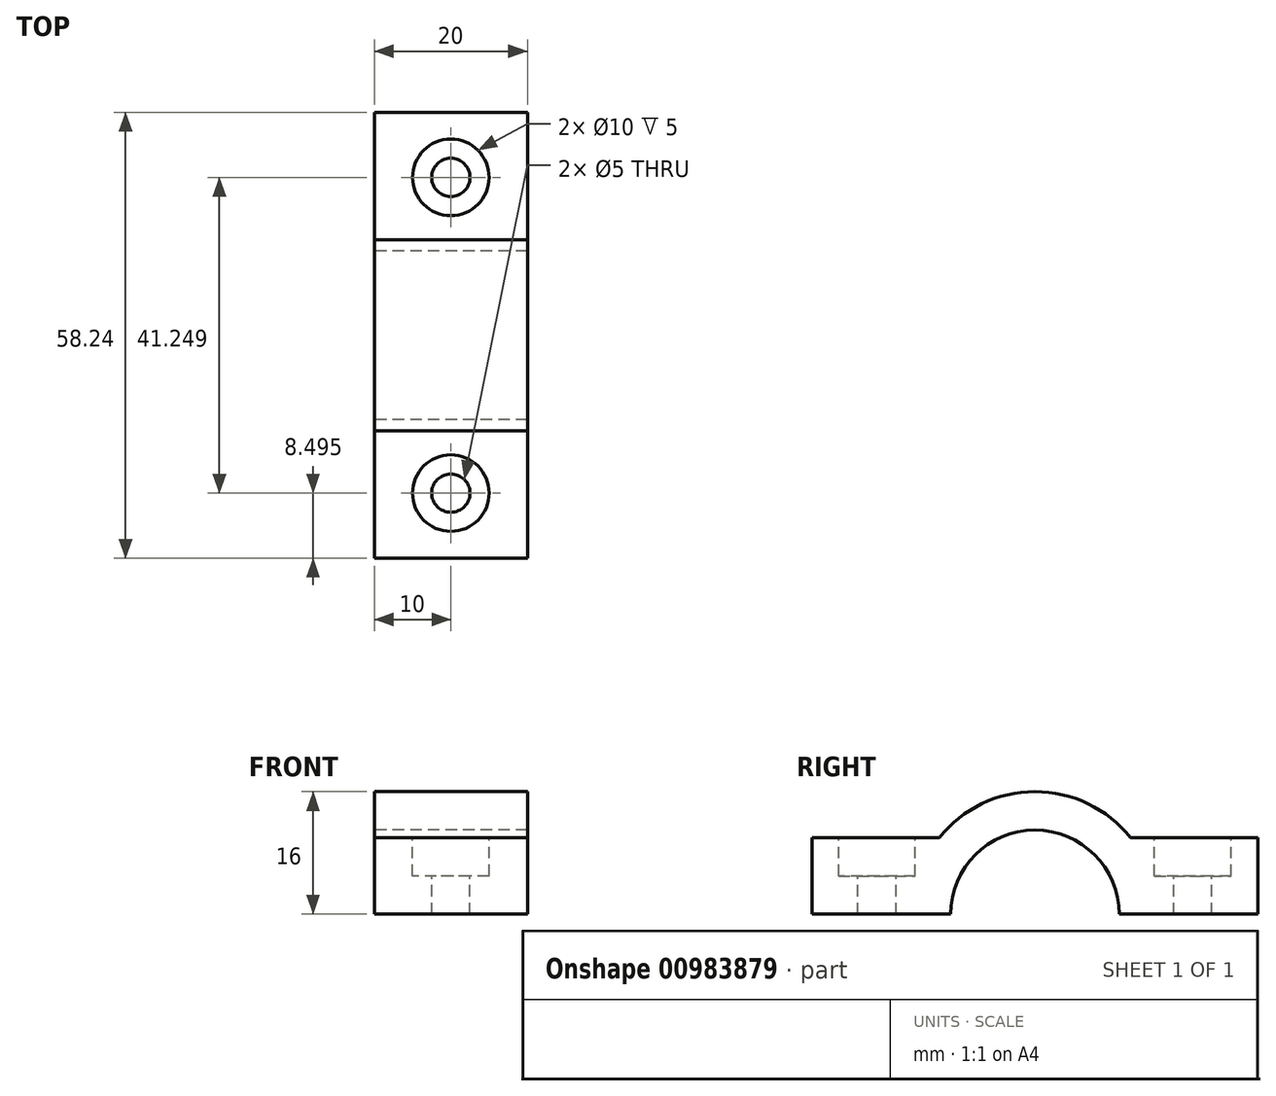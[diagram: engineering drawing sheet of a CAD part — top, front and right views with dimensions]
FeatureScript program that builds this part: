
annotation { "Feature Type Name" : "Feature", "Feature Type Description" : "" }
export const myFeature = defineFeature(function(context is Context, id is Id, definition is map)
    precondition{}
    {
        {
            var Q0;
            Q0=qCreatedBy(makeId("Right.planeOp"),FACE);
            var sketch = newSketch(context, id + "F0", { "sketchPlane" : qUnion([Q0])});
            skArc(sketch, "E0", {"start": v(11, 0) * mm, "mid": v(0, 11) * mm, "end": v(-11, 0) * mm});
            skLineSegment(sketch, "E1", {"start": v(11, 0) * mm, "end": v(29.12, 0) * mm});
            skLineSegment(sketch, "E2", {"start": v(-11, 0) * mm, "end": v(-29.12, 0) * mm});
            skLineSegment(sketch, "E3", {"start": v(29.12, 0) * mm, "end": v(29.12, 10) * mm});
            skLineSegment(sketch, "E4", {"start": v(-29.12, 0) * mm, "end": v(-29.12, 10) * mm});
            skLineSegment(sketch, "E5", {"start": v(-29.12, 10) * mm, "end": v(-12.49, 10) * mm});
            skLineSegment(sketch, "E6.trimOffspring", {"start": v(12.49, 10) * mm, "end": v(29.12, 10) * mm});
            skArc(sketch, "E7.trimOffspring", {"start": v(12.49, 10) * mm, "mid": v(0, 16) * mm, "end": v(-12.49, 10) * mm});
            skSolve(sketch);
        }
        {
            var Q0;
            Q0=makeQuery(id+"F0.imprint","IMPRINT",FACE,{"disambiguationData":[TD([[makeQuery(id+"F0.imprint","IMPRINT",EDGE,{"derivedFrom":sQuery(id+"F0.wireOp",EDGE,"E0")}),-1.0]])]});
            extrude(context, id + "F1", {"entities" : qUnion([Q0]), "depth" : 20 * mm, "offsetDistance" : 25 * mm});
        }
        {
            var Q0;
            Q0=makeQuery(id+"F1.opExtrude","SWEPT_FACE",FACE,{"disambiguationData":[OSD([sQuery(id+"F0.wireOp",EDGE,"E5")])]});
            cPlane(context, id + "F2", {"entities" : qUnion([Q0]), "cplaneType" : CPlaneType.OFFSET, "offset" : 0 * mm, "width" : 150 * mm, "height" : 150 * mm});
        }
        {
            var Q0;
            Q0=qCreatedBy(id+"F2.planeOp",FACE);
            var sketch = newSketch(context, id + "F3", { "sketchPlane" : qUnion([Q0])});
            skLineSegment(sketch, "E8", {"start": v(10, -29.3) * mm, "end": v(10, -20.62) * mm});
            skCircle(sketch, "E9", {"center": v(10, -20.62) * mm, "radius": 2.5 * mm});
            skCircle(sketch, "E10", {"center": v(10, -20.62) * mm, "radius": 5 * mm});
            skSolve(sketch);
        }
        {
            var Q0;
            Q0=makeQuery(id+"F3.imprint","IMPRINT",FACE,{"disambiguationData":[TD([[makeQuery(id+"F3.imprint","IMPRINT",EDGE,{"derivedFrom":sQuery(id+"F3.wireOp",EDGE,"E9")}),-1.0]])]});
            extrude(context, id + "F4", {"entities" : qUnion([Q0]), "operationType" : NewBodyOperationType.REMOVE, "oppositeDirection" : true, "depth" : 5 * mm, "offsetDistance" : 25 * mm});
        }
        {
            var Q0;
            Q0=makeQuery(id+"F3.imprint","IMPRINT",FACE,{"disambiguationData":[TD([[makeQuery(id+"F3.imprint","IMPRINT",EDGE,{"derivedFrom":sQuery(id+"F3.wireOp",EDGE,"E9")}),1.0]])]});
            extrude(context, id + "F5", {"entities" : qUnion([Q0]), "operationType" : NewBodyOperationType.REMOVE, "oppositeDirection" : true, "depth" : 25 * mm, "offsetDistance" : 25 * mm});
        }
        {
            var Q0;
            Q0=makeQuery(id+"F1.opExtrude","SWEPT_FACE",FACE,{"disambiguationData":[OSD([sQuery(id+"F0.wireOp",EDGE,"E6.trimOffspring")])]});
            cPlane(context, id + "F6", {"entities" : qUnion([Q0]), "cplaneType" : CPlaneType.OFFSET, "offset" : 0 * mm, "width" : 150 * mm, "height" : 150 * mm});
        }
        {
            var Q0;
            Q0=qCreatedBy(id+"F6.planeOp",FACE);
            var sketch = newSketch(context, id + "F7", { "sketchPlane" : qUnion([Q0])});
            skLineSegment(sketch, "E11", {"start": v(10, 29.16) * mm, "end": v(10, 20.62) * mm});
            skCircle(sketch, "E12", {"center": v(10, 20.62) * mm, "radius": 5 * mm});
            skCircle(sketch, "E13", {"center": v(10, 20.62) * mm, "radius": 2.5 * mm});
            skSolve(sketch);
        }
        {
            var Q0;
            Q0=makeQuery(id+"F7.imprint","IMPRINT",FACE,{"disambiguationData":[TD([[makeQuery(id+"F7.imprint","IMPRINT",EDGE,{"derivedFrom":sQuery(id+"F7.wireOp",EDGE,"E12")}),1.0]])]});
            extrude(context, id + "F8", {"entities" : qUnion([Q0]), "operationType" : NewBodyOperationType.REMOVE, "oppositeDirection" : true, "depth" : 5 * mm, "offsetDistance" : 25 * mm});
        }
        {
            var Q0;
            Q0=makeQuery(id+"F8.boolean.opBoolean","SPLIT",FACE,{"disambiguationData":[TD([makeQuery(id+"F8.opExtrude","SWEPT_FACE",FACE,{"disambiguationData":[OSD([sQuery(id+"F7.wireOp",EDGE,"E13")])]})])],"derivedFrom":makeQuery(id+"F1.opExtrude","SWEPT_FACE",FACE,{"disambiguationData":[OSD([sQuery(id+"F0.wireOp",EDGE,"E6.trimOffspring")])]})});
            extrude(context, id + "F9", {"entities" : qUnion([Q0]), "operationType" : NewBodyOperationType.REMOVE, "oppositeDirection" : true, "depth" : 25 * mm, "offsetDistance" : 25 * mm});
        }
    });
